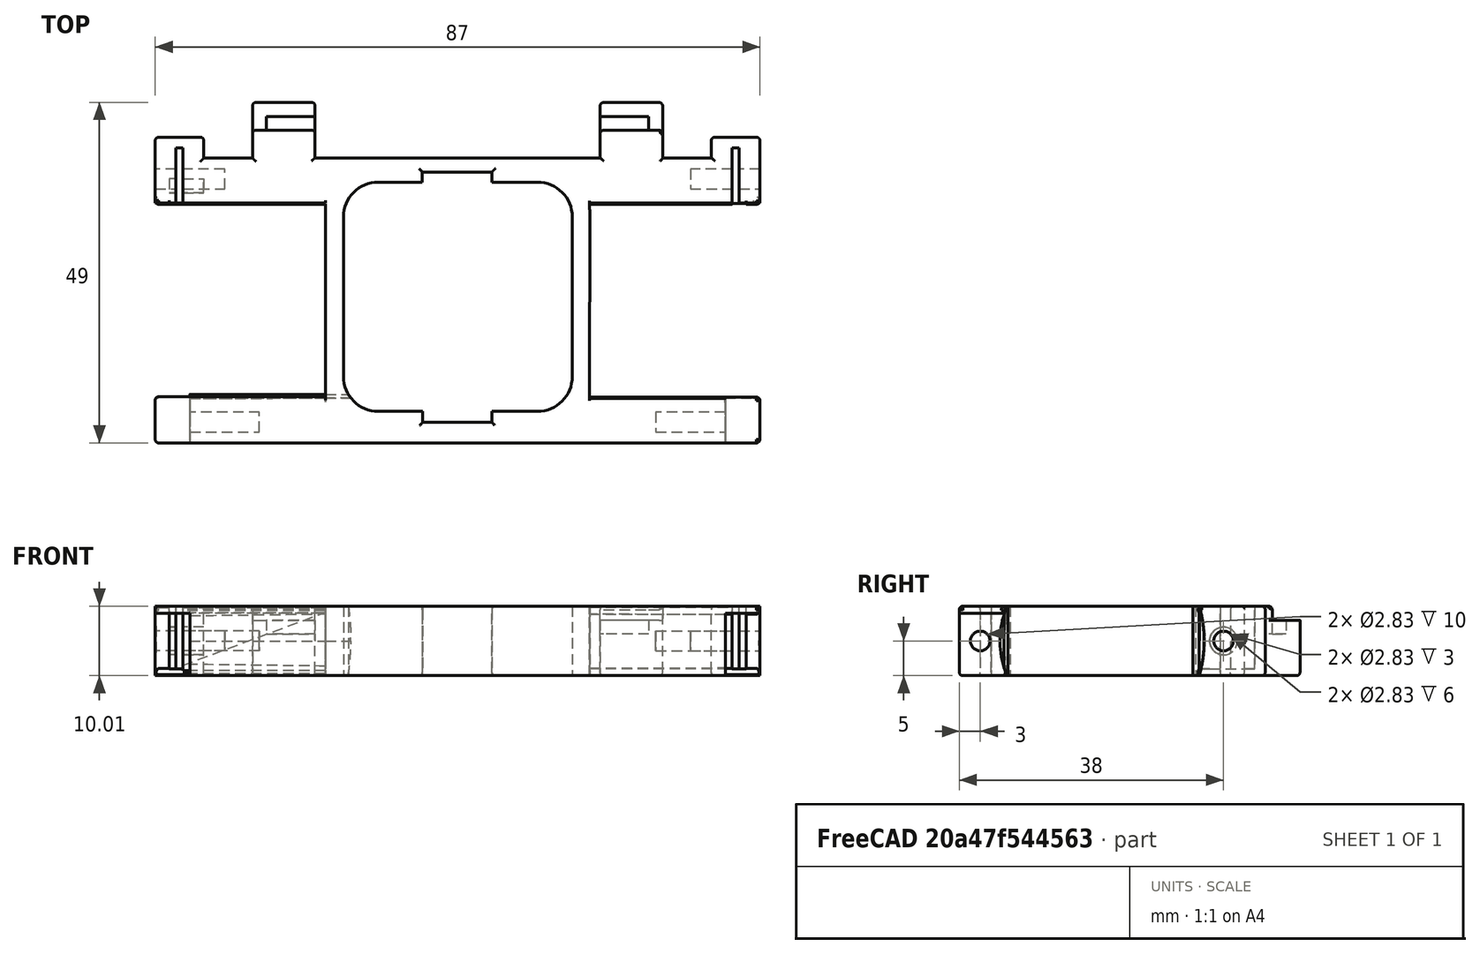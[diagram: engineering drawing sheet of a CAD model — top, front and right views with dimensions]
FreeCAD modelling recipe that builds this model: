
FCSTD DOCUMENT  (FreeCAD 0.18R16110 (Git))
Label: sop_motores
License: All rights reserved
LicenseURL: http://en.wikipedia.org/wiki/All_rights_reserved
objects: PartDesign::Fillet×64, Sketcher::SketchObject×41, PartDesign::Pocket×25, PartDesign::Pad×13, PartDesign::Body×1
note: 182 computed .brp shape members not serialized (recipe doc carries the construction recipe); baked Part::Feature solids carry a one-line shape summary decoded from their .brp

FEATURE [Sketcher::SketchObject] Sketch
  MapMode = 5
  Support = -> [XY_Plane]
  sketch-geometry (24):
    g0: LineSegment StartX=0 StartY=0 StartZ=0 EndX=7 EndY=0 EndZ=0
    g1: LineSegment StartX=7 StartY=0 StartZ=0 EndX=7 EndY=-3 EndZ=0
    g2: LineSegment StartX=7 StartY=-3 StartZ=0 EndX=14 EndY=-3 EndZ=0
    g3: LineSegment StartX=14 StartY=-3 StartZ=0 EndX=14 EndY=5 EndZ=0
    g4: LineSegment StartX=14 StartY=5 StartZ=0 EndX=23 EndY=5 EndZ=0
    g5: LineSegment StartX=23 StartY=5 StartZ=0 EndX=23 EndY=-3 EndZ=0
    g6: LineSegment StartX=23 StartY=-3 StartZ=0 EndX=64 EndY=-3 EndZ=0
    g7: LineSegment StartX=64 StartY=-3 StartZ=0 EndX=64 EndY=5 EndZ=0
    g8: LineSegment StartX=64 StartY=5 StartZ=0 EndX=73 EndY=5 EndZ=0
    g9: LineSegment StartX=73 StartY=5 StartZ=0 EndX=73 EndY=-3 EndZ=0
    g10: LineSegment StartX=73 StartY=-3 StartZ=0 EndX=80 EndY=-3 EndZ=0
    g11: LineSegment StartX=80 StartY=-3 StartZ=0 EndX=80 EndY=0 EndZ=0
    g12: LineSegment StartX=80 StartY=0 StartZ=0 EndX=87 EndY=0 EndZ=0
    g13: LineSegment StartX=87 StartY=0 StartZ=0 EndX=87 EndY=-10 EndZ=0
    g14: LineSegment StartX=87 StartY=-10 StartZ=0 EndX=62.5198 EndY=-10 EndZ=0
    g15: LineSegment StartX=62.4973 StartY=-37 StartZ=0 EndX=87 EndY=-37 EndZ=0
    g16: LineSegment StartX=87 StartY=-37 StartZ=0 EndX=87 EndY=-44 EndZ=0
    g17: LineSegment StartX=87 StartY=-44 StartZ=0 EndX=0 EndY=-44 EndZ=0
    g18: LineSegment StartX=0 StartY=-44 StartZ=0 EndX=0 EndY=-37 EndZ=0
    g19: LineSegment StartX=0 StartY=-37 StartZ=0 EndX=24.4807 EndY=-37 EndZ=0
    g20: LineSegment StartX=24.4807 StartY=-37 StartZ=0 EndX=24.5011 EndY=-10 EndZ=0
    g21: LineSegment StartX=24.5011 StartY=-10 StartZ=0 EndX=0 EndY=-10 EndZ=0
    g22: LineSegment StartX=62.5198 StartY=-10 StartZ=0 EndX=62.4973 EndY=-37 EndZ=0
    g23: LineSegment StartX=0 StartY=0 StartZ=0 EndX=0 EndY=-10 EndZ=0
  constraints (24):
    c: Coincident(g0,g1)
    c: Coincident(g1,g2)
    c: Coincident(g2,g3)
    c: Coincident(g3,g4)
    c: Coincident(g4,g5)
    c: Coincident(g5,g6)
    c: Coincident(g7,g8)
    c: Coincident(g8,g9)
    c: Coincident(g9,g10)
    c: Coincident(g10,g11)
    c: Coincident(g11,g12)
    c: Coincident(g12,g13)
    c: Coincident(g13,g14)
    c: Coincident(g15,g16)
    c: Coincident(g16,g17)
    c: Coincident(g18,g19)
    c: Coincident(g19,g20)
    c: Coincident(g20,g21)
    c: Coincident(g7,g6)
    c: Coincident(g17,g18)
    c: Coincident(g14,g22)
    c: Coincident(g15,g22)
    c: Coincident(g0,g23)
    c: Coincident(g21,g23)
FEATURE [PartDesign::Pad] Pad
  Length = 10
  Length2 = 100
  Profile = -> Sketch
  Type = 0
FEATURE [Sketcher::SketchObject] Sketch001
  MapMode = 5
  Placement = pos=(0,0,10) rot=(0,0,1;0rad)
  Support = -> [Pad]
  sketch-geometry (14):
    g0: LineSegment StartX=43.4694 StartY=-41 StartZ=0 EndX=38.4739 EndY=-41 EndZ=0
    g1: LineSegment StartX=38.4739 StartY=-41 StartZ=0 EndX=38.4739 EndY=-38 EndZ=0
    g2: LineSegment StartX=38.4739 StartY=-38 StartZ=0 EndX=28.4617 EndY=-38 EndZ=0
    g3: LineSegment StartX=28.4617 StartY=-38 StartZ=0 EndX=28.469 EndY=-8 EndZ=0
    g4: LineSegment StartX=28.469 StartY=-8 StartZ=0 EndX=38.4371 EndY=-8 EndZ=0
    g5: LineSegment StartX=38.4371 StartY=-8 StartZ=0 EndX=38.4371 EndY=-5 EndZ=0
    g6: LineSegment StartX=38.4371 StartY=-5 StartZ=0 EndX=48.4367 EndY=-5 EndZ=0
    g7: LineSegment StartX=48.4367 StartY=-5 StartZ=0 EndX=48.4367 EndY=-8 EndZ=0
    g8: LineSegment StartX=48.4367 StartY=-8 StartZ=0 EndX=58.4048 EndY=-8 EndZ=0
    g9: LineSegment StartX=58.4048 StartY=-8 StartZ=0 EndX=58.4159 EndY=-38 EndZ=0
    g10: LineSegment StartX=58.4159 StartY=-38 StartZ=0 EndX=48.4478 EndY=-38 EndZ=0
    g11: LineSegment StartX=48.4478 StartY=-38 StartZ=0 EndX=48.4478 EndY=-41 EndZ=0
    g12: LineSegment StartX=48.4478 StartY=-41 StartZ=0 EndX=43.4166 EndY=-41 EndZ=0
    g13: LineSegment StartX=43.4166 StartY=-41 StartZ=0 EndX=43.4694 EndY=-41 EndZ=0
  constraints (13):
    c: Coincident(g0,g1)
    c: Coincident(g1,g2)
    c: Coincident(g2,g3)
    c: Coincident(g3,g4)
    c: Coincident(g4,g5)
    c: Coincident(g5,g6)
    c: Coincident(g6,g7)
    c: Coincident(g7,g8)
    c: Coincident(g8,g9)
    c: Coincident(g9,g10)
    c: Coincident(g10,g11)
    c: Coincident(g11,g12)
    c: Coincident(g12,g13)
FEATURE [PartDesign::Pocket] Pocket
  BaseFeature = -> Pad
  Length = 10
  Length2 = 100
  Profile = -> Sketch001
  Type = 0
FEATURE [Sketcher::SketchObject] Sketch002
  MapMode = 5
  Placement = pos=(0,0,10) rot=(0,0,1;0rad)
  Support = -> [Pocket]
  sketch-geometry (8):
    g0: LineSegment StartX=23 StartY=1 StartZ=0 EndX=16 EndY=1 EndZ=0
    g1: LineSegment StartX=16 StartY=1 StartZ=0 EndX=16 EndY=3 EndZ=0
    g2: LineSegment StartX=16 StartY=3 StartZ=0 EndX=23 EndY=3 EndZ=0
    g3: LineSegment StartX=23 StartY=3 StartZ=0 EndX=23 EndY=1 EndZ=0
    g4: LineSegment StartX=64 StartY=1 StartZ=0 EndX=71 EndY=1 EndZ=0
    g5: LineSegment StartX=71 StartY=1 StartZ=0 EndX=71 EndY=3 EndZ=0
    g6: LineSegment StartX=71 StartY=3 StartZ=0 EndX=64 EndY=3 EndZ=0
    g7: LineSegment StartX=64 StartY=3 StartZ=0 EndX=64 EndY=1 EndZ=0
  constraints (6):
    c: Coincident(g0,g1)
    c: Coincident(g1,g2)
    c: Coincident(g2,g3)
    c: Coincident(g4,g5)
    c: Coincident(g5,g6)
    c: Coincident(g6,g7)
FEATURE [PartDesign::Pocket] Pocket001
  BaseFeature = -> Pocket
  Length = 5
  Length2 = 100
  Profile = -> Sketch002
  Type = 0
FEATURE [Sketcher::SketchObject] Sketch003
  MapMode = 5
  Placement = pos=(0,5,0) rot=(0,0.707107,0.707107;3.14159rad)
  Support = -> [Pocket001]
  sketch-geometry (8):
    g0: LineSegment StartX=-73 StartY=10 StartZ=0 EndX=-73 EndY=8 EndZ=0
    g1: LineSegment StartX=-73 StartY=8 StartZ=0 EndX=-64 EndY=8 EndZ=0
    g2: LineSegment StartX=-64 StartY=8 StartZ=0 EndX=-64 EndY=10 EndZ=0
    g3: LineSegment StartX=-64 StartY=10 StartZ=0 EndX=-73 EndY=10 EndZ=0
    g4: LineSegment StartX=-23 StartY=10 StartZ=0 EndX=-14 EndY=10 EndZ=0
    g5: LineSegment StartX=-14 StartY=10 StartZ=0 EndX=-14 EndY=8 EndZ=0
    g6: LineSegment StartX=-14 StartY=8 StartZ=0 EndX=-23 EndY=8 EndZ=0
    g7: LineSegment StartX=-23 StartY=8 StartZ=0 EndX=-23 EndY=10 EndZ=0
  constraints (8):
    c: Coincident(g0,g1)
    c: Coincident(g1,g2)
    c: Coincident(g2,g3)
    c: Coincident(g3,g0)
    c: Coincident(g4,g5)
    c: Coincident(g5,g6)
    c: Coincident(g6,g7)
    c: Coincident(g7,g4)
FEATURE [PartDesign::Pocket] Pocket002
  BaseFeature = -> Pocket001
  Length = 4
  Length2 = 100
  Profile = -> Sketch003
  Type = 0
FEATURE [Sketcher::SketchObject] Sketch004
  MapMode = 5
  Placement = pos=(87,0,0) rot=(0.57735,0.57735,0.57735;2.0944rad)
  Support = -> [Pocket002]
  sketch-geometry (2):
    g0: Circle CenterX=-6 CenterY=5 CenterZ=0 NormalX=0 NormalY=0 NormalZ=1 AngleXU=0 Radius=2
    g1: Circle CenterX=-41 CenterY=5 CenterZ=0 NormalX=0 NormalY=0 NormalZ=1 AngleXU=0 Radius=1.97023
FEATURE [PartDesign::Pocket] Pocket003
  BaseFeature = -> Pocket002
  Length = 12
  Length2 = 100
  Profile = -> Sketch004
  Type = 0
FEATURE [Sketcher::SketchObject] Sketch005
  MapMode = 5
  Placement = pos=(0,0,0) rot=(0.57735,-0.57735,-0.57735;2.0944rad)
  Support = -> [Pocket003]
  sketch-geometry (2):
    g0: Circle CenterX=6 CenterY=5 CenterZ=0 NormalX=0 NormalY=0 NormalZ=1 AngleXU=0 Radius=2
    g1: Circle CenterX=41 CenterY=5 CenterZ=0 NormalX=0 NormalY=0 NormalZ=1 AngleXU=0 Radius=2
FEATURE [PartDesign::Pocket] Pocket004
  BaseFeature = -> Pocket003
  Length = 12
  Length2 = 100
  Profile = -> Sketch005
  Type = 0
FEATURE [Sketcher::SketchObject] Sketch006
  MapMode = 5
  Placement = pos=(87,0,0) rot=(0.57735,0.57735,0.57735;2.0944rad)
  Support = -> [Pocket004]
  sketch-geometry (2):
    g0: ArcOfCircle CenterX=-24.8709 CenterY=5 CenterZ=0 NormalX=0 NormalY=0 NormalZ=1 AngleXU=0 Radius=13.2724 StartAngle=2.67251 EndAngle=3.61067
    g1: LineSegment StartX=-36.7097 StartY=11 StartZ=0 EndX=-36.7097 EndY=-0.999998 EndZ=0
  constraints (2):
    c: Coincident(g0,g1)
    c: Coincident(g0,g1)
FEATURE [PartDesign::Pocket] Pocket005
  BaseFeature = -> Pocket004
  Length = 24.5
  Length2 = 100
  Profile = -> Sketch006
  Type = 0
FEATURE [Sketcher::SketchObject] Sketch007
  MapMode = 5
  Placement = pos=(87,0,0) rot=(0.57735,0.57735,0.57735;2.0944rad)
  Support = -> [Pocket005]
  sketch-geometry (2):
    g0: ArcOfCircle CenterX=-22.2977 CenterY=5 CenterZ=0 NormalX=0 NormalY=0 NormalZ=1 AngleXU=0 Radius=13.3937 StartAngle=5.80677 EndAngle=6.75968
    g1: LineSegment StartX=-10.396 StartY=11.1433 StartZ=0 EndX=-10.3955 EndY=-1.14226 EndZ=0
  constraints (2):
    c: Coincident(g0,g1)
    c: Coincident(g0,g1)
FEATURE [PartDesign::Pocket] Pocket006
  BaseFeature = -> Pocket005
  Length = 24.5
  Length2 = 100
  Profile = -> Sketch007
  Type = 0
FEATURE [Sketcher::SketchObject] Sketch008
  MapMode = 5
  Placement = pos=(0,0,0) rot=(0.57735,-0.57735,-0.57735;2.0944rad)
  Support = -> [Pocket006]
  sketch-geometry (2):
    g0: ArcOfCircle CenterX=22.1388 CenterY=5.06289 CenterZ=0 NormalX=0 NormalY=0 NormalZ=1 AngleXU=0 Radius=13.2617 StartAngle=2.6721 EndAngle=3.61108
    g1: LineSegment StartX=10.312 StartY=11.0629 StartZ=0 EndX=10.312 EndY=-0.93711 EndZ=0
  constraints (2):
    c: Coincident(g0,g1)
    c: Coincident(g0,g1)
FEATURE [PartDesign::Pocket] Pocket007
  BaseFeature = -> Pocket006
  Length = 24.5
  Length2 = 100
  Profile = -> Sketch008
  Type = 0
FEATURE [Sketcher::SketchObject] Sketch009
  MapMode = 5
  Placement = pos=(0,0,0) rot=(0.57735,-0.57735,-0.57735;2.0944rad)
  Support = -> [Pocket007]
  sketch-geometry (2):
    g0: ArcOfCircle CenterX=24.8808 CenterY=5 CenterZ=0 NormalX=0 NormalY=0 NormalZ=1 AngleXU=0 Radius=13.2314 StartAngle=5.81253 EndAngle=6.75384
    g1: LineSegment StartX=36.6736 StartY=11 StartZ=0 EndX=36.6736 EndY=-1 EndZ=0
  constraints (2):
    c: Coincident(g0,g1)
    c: Coincident(g0,g1)
FEATURE [PartDesign::Pocket] Pocket008
  BaseFeature = -> Pocket007
  Length = 24.5
  Length2 = 100
  Profile = -> Sketch009
  Type = 0
FEATURE [Sketcher::SketchObject] Sketch010
  MapMode = 5
  Placement = pos=(0,0,10) rot=(0,0,1;0rad)
  Support = -> [Pocket008]
  sketch-geometry (8):
    g0: LineSegment StartX=2 StartY=-10 StartZ=0 EndX=4 EndY=-10 EndZ=0
    g1: LineSegment StartX=4 StartY=-10 StartZ=0 EndX=4 EndY=-3 EndZ=0
    g2: LineSegment StartX=4 StartY=-3 StartZ=0 EndX=2 EndY=-3 EndZ=0
    g3: LineSegment StartX=2 StartY=-3 StartZ=0 EndX=2 EndY=-10 EndZ=0
    g4: LineSegment StartX=83 StartY=-10 StartZ=0 EndX=85 EndY=-10 EndZ=0
    g5: LineSegment StartX=85 StartY=-10 StartZ=0 EndX=85 EndY=-3 EndZ=0
    g6: LineSegment StartX=85 StartY=-3 StartZ=0 EndX=83 EndY=-3 EndZ=0
    g7: LineSegment StartX=83 StartY=-3 StartZ=0 EndX=83 EndY=-10 EndZ=0
  constraints (8):
    c: Coincident(g0,g1)
    c: Coincident(g1,g2)
    c: Coincident(g2,g3)
    c: Coincident(g3,g0)
    c: Coincident(g4,g5)
    c: Coincident(g5,g6)
    c: Coincident(g6,g7)
    c: Coincident(g7,g4)
FEATURE [PartDesign::Pocket] Pocket009
  BaseFeature = -> Pocket008
  Length = 9
  Length2 = 100
  Profile = -> Sketch010
  Type = 0
FEATURE [PartDesign::Fillet] Fillet
  Base = -> Pocket009 [Edge64]
  BaseFeature = -> Pocket009
  Radius = 0.5
FEATURE [PartDesign::Fillet] Fillet001
  Base = -> Fillet [Edge7]
  BaseFeature = -> Fillet
  Radius = 0.5
FEATURE [PartDesign::Fillet] Fillet002
  Base = -> Fillet001 [Edge3]
  BaseFeature = -> Fillet001
  Radius = 0.5
FEATURE [PartDesign::Fillet] Fillet003
  Base = -> Fillet002 [Edge51]
  BaseFeature = -> Fillet002
  Radius = 0.5
FEATURE [PartDesign::Fillet] Fillet004
  Base = -> Fillet003 [Edge14]
  BaseFeature = -> Fillet003
  Radius = 0.5
FEATURE [PartDesign::Fillet] Fillet005
  Base = -> Fillet004 [Edge17]
  BaseFeature = -> Fillet004
  Radius = 0.5
FEATURE [PartDesign::Fillet] Fillet006
  Base = -> Fillet005 [Edge9]
  BaseFeature = -> Fillet005
  Radius = 0.4
FEATURE [PartDesign::Fillet] Fillet007
  Base = -> Fillet006 [Edge7]
  BaseFeature = -> Fillet006
  Radius = 0.4
FEATURE [PartDesign::Fillet] Fillet008
  Base = -> Fillet007 [Edge10]
  BaseFeature = -> Fillet007
  Radius = 0.4
FEATURE [PartDesign::Fillet] Fillet009
  Base = -> Fillet008 [Edge8]
  BaseFeature = -> Fillet008
  Radius = 0.5
FEATURE [PartDesign::Fillet] Fillet010
  Base = -> Fillet009 [Edge21]
  BaseFeature = -> Fillet009
  Radius = 0.5
FEATURE [PartDesign::Fillet] Fillet011
  Base = -> Fillet010 [Edge1]
  BaseFeature = -> Fillet010
  Radius = 0.5
FEATURE [PartDesign::Fillet] Fillet012
  Base = -> Fillet011 [Edge6]
  BaseFeature = -> Fillet011
  Radius = 0.5
FEATURE [PartDesign::Fillet] Fillet013
  Base = -> Fillet012 [Edge9]
  BaseFeature = -> Fillet012
  Radius = 0.5
FEATURE [PartDesign::Fillet] Fillet014
  Base = -> Fillet013 [Edge1]
  BaseFeature = -> Fillet013
  Radius = 0.4
FEATURE [PartDesign::Fillet] Fillet015
  Base = -> Fillet014 [Edge28]
  BaseFeature = -> Fillet014
  Radius = 0.54
FEATURE [PartDesign::Fillet] Fillet016
  Base = -> Fillet015 [Edge3]
  BaseFeature = -> Fillet015
  Radius = 0.5
FEATURE [PartDesign::Fillet] Fillet017
  Base = -> Fillet016 [Edge18]
  BaseFeature = -> Fillet016
  Radius = 0.5
FEATURE [PartDesign::Fillet] Fillet018
  Base = -> Fillet017 [Edge26]
  BaseFeature = -> Fillet017
  Radius = 0.5
FEATURE [PartDesign::Fillet] Fillet019
  Base = -> Fillet018 [Edge41]
  BaseFeature = -> Fillet018
  Radius = 0.5
FEATURE [PartDesign::Fillet] Fillet020
  Base = -> Fillet019 [Edge31]
  BaseFeature = -> Fillet019
  Radius = 0.5
FEATURE [PartDesign::Fillet] Fillet021
  Base = -> Fillet020 [Edge29]
  BaseFeature = -> Fillet020
  Radius = 0.5
FEATURE [PartDesign::Fillet] Fillet022
  Base = -> Fillet021 [Edge1]
  BaseFeature = -> Fillet021
  Radius = 0.5
FEATURE [PartDesign::Fillet] Fillet023
  Base = -> Fillet022 [Edge6]
  BaseFeature = -> Fillet022
  Radius = 0.5
FEATURE [PartDesign::Fillet] Fillet024
  Base = -> Fillet023 [Edge9]
  BaseFeature = -> Fillet023
  Radius = 0.5
FEATURE [PartDesign::Fillet] Fillet025
  Base = -> Fillet024 [Edge3]
  BaseFeature = -> Fillet024
  Radius = 0.5
FEATURE [PartDesign::Fillet] Fillet026
  Base = -> Fillet025 [Edge6]
  BaseFeature = -> Fillet025
  Radius = 0.5
FEATURE [PartDesign::Fillet] Fillet027
  Base = -> Fillet026 [Edge8]
  BaseFeature = -> Fillet026
  Radius = 0.5
FEATURE [PartDesign::Fillet] Fillet028
  Base = -> Fillet027 [Edge11]
  BaseFeature = -> Fillet027
  Radius = 0.5
FEATURE [PartDesign::Fillet] Fillet029
  Base = -> Fillet028 [Edge1]
  BaseFeature = -> Fillet028
  Radius = 0.5
FEATURE [PartDesign::Fillet] Fillet030
  Base = -> Fillet029 [Edge6]
  BaseFeature = -> Fillet029
  Radius = 0.4
FEATURE [PartDesign::Fillet] Fillet031
  Base = -> Fillet030 [Edge2]
  BaseFeature = -> Fillet030
  Radius = 0.3
FEATURE [PartDesign::Fillet] Fillet032
  Base = -> Fillet031 [Edge3]
  BaseFeature = -> Fillet031
  Radius = 0.5
FEATURE [PartDesign::Fillet] Fillet033
  Base = -> Fillet032 [Edge10]
  BaseFeature = -> Fillet032
  Radius = 0.4
FEATURE [PartDesign::Fillet] Fillet034
  Base = -> Fillet033 [Edge152]
  BaseFeature = -> Fillet033
  Radius = 0.5
FEATURE [PartDesign::Fillet] Fillet035
  Base = -> Fillet034 [Edge12]
  BaseFeature = -> Fillet034
  Radius = 0.5
FEATURE [PartDesign::Fillet] Fillet036
  Base = -> Fillet035 [Edge71]
  BaseFeature = -> Fillet035
  Radius = 0.5
FEATURE [PartDesign::Fillet] Fillet037
  Base = -> Fillet036 [Edge1]
  BaseFeature = -> Fillet036
  Radius = 0.5
FEATURE [PartDesign::Fillet] Fillet038
  Base = -> Fillet037 [Edge24]
  BaseFeature = -> Fillet037
  Radius = 0.5
FEATURE [PartDesign::Fillet] Fillet039
  Base = -> Fillet038 [Edge3]
  BaseFeature = -> Fillet038
  Radius = 0.5
FEATURE [PartDesign::Fillet] Fillet040
  Base = -> Fillet039 [Edge8]
  BaseFeature = -> Fillet039
  Radius = 0.5
FEATURE [PartDesign::Fillet] Fillet041
  Base = -> Fillet040 [Edge3]
  BaseFeature = -> Fillet040
  Radius = 0.5
FEATURE [PartDesign::Fillet] Fillet042
  Base = -> Fillet041 [Edge6]
  BaseFeature = -> Fillet041
  Radius = 0.4
FEATURE [PartDesign::Fillet] Fillet043
  Base = -> Fillet042 [Edge31]
  BaseFeature = -> Fillet042
  Radius = 0.4
FEATURE [PartDesign::Fillet] Fillet044
  Base = -> Fillet043 [Edge4]
  BaseFeature = -> Fillet043
  Radius = 0.5
FEATURE [PartDesign::Fillet] Fillet045
  Base = -> Fillet044 [Edge14]
  BaseFeature = -> Fillet044
  Radius = 0.5
FEATURE [PartDesign::Fillet] Fillet046
  Base = -> Fillet045 [Edge61]
  BaseFeature = -> Fillet045
  Radius = 0.5
FEATURE [PartDesign::Fillet] Fillet047
  Base = -> Fillet046 [Edge16]
  BaseFeature = -> Fillet046
  Radius = 0.5
FEATURE [PartDesign::Fillet] Fillet048
  Base = -> Fillet047 [Edge26]
  BaseFeature = -> Fillet047
  Radius = 0.4
FEATURE [PartDesign::Fillet] Fillet049
  Base = -> Fillet048 [Edge62]
  BaseFeature = -> Fillet048
  Radius = 0.5
FEATURE [PartDesign::Fillet] Fillet050
  Base = -> Fillet049 [Edge6]
  BaseFeature = -> Fillet049
  Radius = 0.5
FEATURE [PartDesign::Fillet] Fillet051
  Base = -> Fillet050 [Edge16]
  BaseFeature = -> Fillet050
  Radius = 0.49
FEATURE [PartDesign::Fillet] Fillet052
  Base = -> Fillet051 [Edge15]
  BaseFeature = -> Fillet051
  Radius = 0.49
FEATURE [PartDesign::Fillet] Fillet053
  Base = -> Fillet052 [Edge13]
  BaseFeature = -> Fillet052
  Radius = 0.39
FEATURE [PartDesign::Fillet] Fillet054
  Base = -> Fillet053 [Edge26]
  BaseFeature = -> Fillet053
  Radius = 0.39
FEATURE [PartDesign::Fillet] Fillet055
  Base = -> Fillet054 [Edge69]
  BaseFeature = -> Fillet054
  Radius = 0.5
FEATURE [Sketcher::SketchObject] Sketch011
  MapMode = 5
  Placement = pos=(0,0,0) rot=(1,0,0;3.14159rad)
  Support = -> [Fillet055]
  sketch-geometry (8):
    g0: LineSegment StartX=0 StartY=44 StartZ=0 EndX=1 EndY=44 EndZ=0
    g1: LineSegment StartX=1 StartY=44 StartZ=0 EndX=1 EndY=37 EndZ=0
    g2: LineSegment StartX=1 StartY=37 StartZ=0 EndX=0 EndY=37 EndZ=0
    g3: LineSegment StartX=0 StartY=37 StartZ=0 EndX=0 EndY=44 EndZ=0
    g4: LineSegment StartX=86 StartY=44 StartZ=0 EndX=87 EndY=44 EndZ=0
    g5: LineSegment StartX=87 StartY=44 StartZ=0 EndX=87 EndY=37 EndZ=0
    g6: LineSegment StartX=87 StartY=37 StartZ=0 EndX=86 EndY=37 EndZ=0
    g7: LineSegment StartX=86 StartY=37 StartZ=0 EndX=86 EndY=44 EndZ=0
  constraints (8):
    c: Coincident(g0,g1)
    c: Coincident(g1,g2)
    c: Coincident(g2,g3)
    c: Coincident(g3,g0)
    c: Coincident(g4,g5)
    c: Coincident(g5,g6)
    c: Coincident(g6,g7)
    c: Coincident(g7,g4)
FEATURE [PartDesign::Pocket] Pocket010
  BaseFeature = -> Fillet055
  Length = 9
  Length2 = 100
  Profile = -> Sketch011
  Type = 0
FEATURE [PartDesign::Fillet] Fillet056
  Base = -> Pocket010 [Edge442]
  BaseFeature = -> Pocket010
  Radius = 5
FEATURE [PartDesign::Fillet] Fillet057
  Base = -> Fillet056 [Edge461]
  BaseFeature = -> Fillet056
  Radius = 5
FEATURE [PartDesign::Fillet] Fillet058
  Base = -> Fillet057 [Edge477]
  BaseFeature = -> Fillet057
  Radius = 5
FEATURE [PartDesign::Fillet] Fillet059
  Base = -> Fillet058 [Edge487]
  BaseFeature = -> Fillet058
  Radius = 5
FEATURE [Sketcher::SketchObject] Sketch012
  MapMode = 5
  Placement = pos=(0,0,10) rot=(0,0,1;0rad)
  Support = -> [Fillet059]
  sketch-geometry (4):
    g0: LineSegment StartX=27.0787 StartY=-6.46494 StartZ=0 EndX=60 EndY=-6.46494 EndZ=0
    g1: LineSegment StartX=60 StartY=-6.46494 StartZ=0 EndX=60 EndY=-39.4522 EndZ=0
    g2: LineSegment StartX=60 StartY=-39.4522 StartZ=0 EndX=27.0787 EndY=-39.4522 EndZ=0
    g3: LineSegment StartX=27.0787 StartY=-39.4522 StartZ=0 EndX=27.0787 EndY=-6.46494 EndZ=0
  constraints (8):
    c: Coincident(g0,g1)
    c: Coincident(g1,g2)
    c: Coincident(g2,g3)
    c: Coincident(g3,g0)
    c: Horizontal(g0)
    c: Horizontal(g2)
    c: Vertical(g1)
    c: Vertical(g3)
FEATURE [PartDesign::Pocket] Pocket011
  BaseFeature = -> Fillet059
  Length = 10
  Length2 = 100
  Profile = -> Sketch012
  Type = 0
FEATURE [PartDesign::Fillet] Fillet060
  Base = -> Pocket011 [Edge187]
  BaseFeature = -> Pocket011
  Radius = 5
FEATURE [PartDesign::Fillet] Fillet061
  Base = -> Fillet060 [Edge107]
  BaseFeature = -> Fillet060
  Radius = 5
FEATURE [PartDesign::Fillet] Fillet062
  Base = -> Fillet061 [Edge114]
  BaseFeature = -> Fillet061
  Radius = 5
FEATURE [PartDesign::Fillet] Fillet063
  Base = -> Fillet062 [Edge117]
  BaseFeature = -> Fillet062
  Radius = 5
FEATURE [Sketcher::SketchObject] Sketch013
  MapMode = 5
  Placement = pos=(0,0,10) rot=(0,0,1;0rad)
  Support = -> [Fillet063]
  sketch-geometry (8):
    g0: LineSegment StartX=2 StartY=-3 StartZ=0 EndX=4 EndY=-3 EndZ=0
    g1: LineSegment StartX=4 StartY=-3 StartZ=0 EndX=4 EndY=-1.53185 EndZ=0
    g2: LineSegment StartX=4 StartY=-1.53185 StartZ=0 EndX=2 EndY=-1.53185 EndZ=0
    g3: LineSegment StartX=2 StartY=-1.53185 StartZ=0 EndX=2 EndY=-3 EndZ=0
    g4: LineSegment StartX=83 StartY=-3 StartZ=0 EndX=85 EndY=-3 EndZ=0
    g5: LineSegment StartX=85 StartY=-3 StartZ=0 EndX=85 EndY=-1.50986 EndZ=0
    g6: LineSegment StartX=85 StartY=-1.50986 StartZ=0 EndX=83 EndY=-1.50986 EndZ=0
    g7: LineSegment StartX=83 StartY=-1.50986 StartZ=0 EndX=83 EndY=-3 EndZ=0
  constraints (16):
    c: Coincident(g0,g1)
    c: Coincident(g1,g2)
    c: Coincident(g2,g3)
    c: Coincident(g3,g0)
    c: Horizontal(g0)
    c: Horizontal(g2)
    c: Vertical(g1)
    c: Vertical(g3)
    c: Coincident(g4,g5)
    c: Coincident(g5,g6)
    c: Coincident(g6,g7)
    c: Coincident(g7,g4)
    c: Horizontal(g4)
    c: Horizontal(g6)
    c: Vertical(g5)
    c: Vertical(g7)
FEATURE [PartDesign::Pocket] Pocket012
  BaseFeature = -> Fillet063
  Length = 9
  Length2 = 100
  Profile = -> Sketch013
  Type = 0
FEATURE [Sketcher::SketchObject] Sketch014
  MapMode = 5
  Placement = pos=(1,0,0) rot=(0.57735,-0.57735,-0.57735;2.0944rad)
  Support = -> [Pocket012]
  sketch-geometry (4):
    g0: LineSegment StartX=44 StartY=0 StartZ=0 EndX=44 EndY=9 EndZ=0
    g1: LineSegment StartX=44 StartY=9 StartZ=0 EndX=37 EndY=9 EndZ=0
    g2: LineSegment StartX=37 StartY=9 StartZ=0 EndX=37 EndY=0 EndZ=0
    g3: LineSegment StartX=37 StartY=0 StartZ=0 EndX=44 EndY=0 EndZ=0
  constraints (4):
    c: Coincident(g0,g1)
    c: Coincident(g1,g2)
    c: Coincident(g2,g3)
    c: Coincident(g3,g0)
FEATURE [PartDesign::Pocket] Pocket013
  BaseFeature = -> Pocket012
  Length = 4
  Length2 = 100
  Profile = -> Sketch014
  Type = 0
FEATURE [Sketcher::SketchObject] Sketch015
  MapMode = 5
  Placement = pos=(86,0,0) rot=(0.57735,0.57735,0.57735;2.0944rad)
  Support = -> [Pocket013]
  sketch-geometry (4):
    g0: LineSegment StartX=-44 StartY=9 StartZ=0 EndX=-37 EndY=9 EndZ=0
    g1: LineSegment StartX=-37 StartY=9 StartZ=0 EndX=-37 EndY=0 EndZ=0
    g2: LineSegment StartX=-37 StartY=0 StartZ=0 EndX=-44 EndY=0 EndZ=0
    g3: LineSegment StartX=-44 StartY=0 StartZ=0 EndX=-44 EndY=9 EndZ=0
  constraints (4):
    c: Coincident(g0,g1)
    c: Coincident(g1,g2)
    c: Coincident(g2,g3)
    c: Coincident(g3,g0)
FEATURE [PartDesign::Pocket] Pocket014
  BaseFeature = -> Pocket013
  Length = 4
  Length2 = 100
  Profile = -> Sketch015
  Type = 0
FEATURE [Sketcher::SketchObject] Sketch016
  MapMode = 5
  Placement = pos=(62.5281,-0.0521484,0) rot=(0.577671,0.57719,0.57719;2.09391rad)
  Support = -> [Pocket014]
  sketch-geometry (2):
    g0: LineSegment StartX=-37.5 StartY=-2.18812e-11 StartZ=0 EndX=-37.5259 EndY=10 EndZ=0
    g1: ArcOfCircle CenterX=-18.8886 CenterY=5.04815 CenterZ=0 NormalX=0 NormalY=0 NormalZ=1 AngleXU=0 Radius=19.2839 StartAngle=2.8819 EndAngle=3.40646
  constraints (2):
    c: Coincident(g1,g0)
    c: Coincident(g0,g1)
FEATURE [PartDesign::Pad] Pad001
  BaseFeature = -> Pocket014
  Length = 19.5
  Length2 = 100
  Profile = -> Sketch016
  Type = 0
FEATURE [Sketcher::SketchObject] Sketch017
  MapMode = 5
  Placement = pos=(62.5,0,0) rot=(0.57735,0.57735,0.57735;2.0944rad)
  Support = -> [Pad001]
  sketch-geometry (2):
    g0: LineSegment StartX=-9.47195 StartY=10 StartZ=0 EndX=-9.5 EndY=-3.1557e-11 EndZ=0
    g1: ArcOfCircle CenterX=-27.0658 CenterY=5.0493 CenterZ=0 NormalX=0 NormalY=0 NormalZ=1 AngleXU=0 Radius=18.2771 StartAngle=6.00328 EndAngle=6.55748
  constraints (2):
    c: Coincident(g0,g1)
    c: Coincident(g0,g1)
FEATURE [PartDesign::Pad] Pad002
  BaseFeature = -> Pad001
  Length = 24.5
  Length2 = 100
  Profile = -> Sketch017
  Type = 0
FEATURE [Sketcher::SketchObject] Sketch018
  MapMode = 5
  Placement = pos=(0,0,10) rot=(0,0,1;0rad)
  Support = -> [Pad002]
  sketch-geometry (4):
    g0: LineSegment StartX=83 StartY=-8 StartZ=0 EndX=85 EndY=-8 EndZ=0
    g1: LineSegment StartX=85 StartY=-8 StartZ=0 EndX=85 EndY=-10 EndZ=0
    g2: LineSegment StartX=85 StartY=-10 StartZ=0 EndX=83 EndY=-10 EndZ=0
    g3: LineSegment StartX=83 StartY=-10 StartZ=0 EndX=83 EndY=-8 EndZ=0
  constraints (4):
    c: Coincident(g0,g1)
    c: Coincident(g1,g2)
    c: Coincident(g2,g3)
    c: Coincident(g3,g0)
FEATURE [PartDesign::Pocket] Pocket015
  BaseFeature = -> Pad002
  Length = 9
  Length2 = 100
  Profile = -> Sketch018
  Type = 0
FEATURE [Sketcher::SketchObject] Sketch019
  MapMode = 5
  Placement = pos=(24.5087,-0.0185195,0) rot=(-0.577059,0.577496,0.577496;4.18835rad)
  Support = -> [Pocket015]
  sketch-geometry (2):
    g0: LineSegment StartX=9.5 StartY=1.8e-15 StartZ=0 EndX=9.47975 EndY=10.0065 EndZ=0
    g1: ArcOfCircle CenterX=24.7722 CenterY=5.03418 CenterZ=0 NormalX=0 NormalY=0 NormalZ=1 AngleXU=0 Radius=16.0805 StartAngle=2.82723 EndAngle=3.46001
  constraints (2):
    c: Coincident(g0,g1)
    c: Coincident(g0,g1)
FEATURE [PartDesign::Pad] Pad003
  BaseFeature = -> Pocket015
  Length = 24.5
  Length2 = 100
  Profile = -> Sketch019
  Type = 0
FEATURE [Sketcher::SketchObject] Sketch020
  MapMode = 5
  Placement = pos=(0,0,10) rot=(0,0,1;0rad)
  Support = -> [Pad003]
  sketch-geometry (4):
    g0: LineSegment StartX=2 StartY=-8 StartZ=0 EndX=4 EndY=-8 EndZ=0
    g1: LineSegment StartX=4 StartY=-8 StartZ=0 EndX=4 EndY=-10 EndZ=0
    g2: LineSegment StartX=4 StartY=-10 StartZ=0 EndX=2 EndY=-10 EndZ=0
    g3: LineSegment StartX=2 StartY=-10 StartZ=0 EndX=2 EndY=-8 EndZ=0
  constraints (4):
    c: Coincident(g0,g1)
    c: Coincident(g1,g2)
    c: Coincident(g2,g3)
    c: Coincident(g3,g0)
FEATURE [PartDesign::Pocket] Pocket016
  BaseFeature = -> Pad003
  Length = 9
  Length2 = 100
  Profile = -> Sketch020
  Type = 0
FEATURE [Sketcher::SketchObject] Sketch021
  MapMode = 5
  Placement = pos=(24.5087,-0.0185195,0) rot=(-0.577059,0.577496,0.577496;4.18835rad)
  Support = -> [Pocket016]
  sketch-geometry (2):
    g0: LineSegment StartX=37 StartY=-3.6e-15 StartZ=0 EndX=37.02 EndY=10.0097 EndZ=0
    g1: ArcOfCircle CenterX=27.1332 CenterY=5.02455 CenterZ=0 NormalX=0 NormalY=0 NormalZ=1 AngleXU=0 Radius=11.0725 StartAngle=5.81217 EndAngle=6.75021
  constraints (2):
    c: Coincident(g1,g0)
    c: Coincident(g1,g0)
FEATURE [PartDesign::Pad] Pad004
  BaseFeature = -> Pocket016
  Length = 19.5
  Length2 = 100
  Profile = -> Sketch021
  Type = 0
FEATURE [Sketcher::SketchObject] Sketch022
  MapMode = 5
  Placement = pos=(0,0,5) rot=(0,0,1;0rad)
  Support = -> [Pad004]
  sketch-geometry (8):
    g0: LineSegment StartX=16 StartY=3 StartZ=0 EndX=16 EndY=0.512637 EndZ=0
    g1: LineSegment StartX=16 StartY=0.512637 StartZ=0 EndX=23 EndY=0.45612 EndZ=0
    g2: LineSegment StartX=23 StartY=0.45612 StartZ=0 EndX=23 EndY=3 EndZ=0
    g3: LineSegment StartX=23 StartY=3 StartZ=0 EndX=16 EndY=3 EndZ=0
    g4: LineSegment StartX=71 StartY=3 StartZ=0 EndX=64 EndY=3 EndZ=0
    g5: LineSegment StartX=64 StartY=3 StartZ=0 EndX=64 EndY=0.483334 EndZ=0
    g6: LineSegment StartX=64 StartY=0.483334 StartZ=0 EndX=71 EndY=0.483334 EndZ=0
    g7: LineSegment StartX=71 StartY=0.483334 StartZ=0 EndX=71 EndY=3 EndZ=0
  constraints (8):
    c: Coincident(g0,g1)
    c: Coincident(g1,g2)
    c: Coincident(g2,g3)
    c: Coincident(g3,g0)
    c: Coincident(g4,g5)
    c: Coincident(g5,g6)
    c: Coincident(g6,g7)
    c: Coincident(g7,g4)
FEATURE [PartDesign::Pad] Pad005
  BaseFeature = -> Pad004
  Length = 1
  Length2 = 100
  Profile = -> Sketch022
  Type = 0
FEATURE [Sketcher::SketchObject] Sketch023
  MapMode = 5
  Placement = pos=(62.5281,-0.0521484,0) rot=(0.577671,0.57719,0.57719;2.09391rad)
  Support = -> [Pad005]
FEATURE [Sketcher::SketchObject] Sketch024
  MapMode = 5
  Placement = pos=(24.5087,-0.0185195,0) rot=(-0.577059,0.577496,0.577496;4.18835rad)
  Support = -> [Pad005]
FEATURE [Sketcher::SketchObject] Sketch025
  MapMode = 5
  Placement = pos=(5.00867,-0.0037847,-1.2e-15) rot=(-0.577059,0.577496,0.577496;4.18835rad)
  Support = -> [Pad005]
  sketch-geometry (3):
    g0: LineSegment StartX=36.99 StartY=0 StartZ=0 EndX=36.9935 EndY=9.99852 EndZ=0
    g1: ArcOfCircle CenterX=16.6778 CenterY=4.56607 CenterZ=0 NormalX=0 NormalY=0 NormalZ=1 AngleXU=0 Radius=20.8191 StartAngle=6.06207 EndAngle=6.30397
    g2: ArcOfCircle CenterX=16.9079 CenterY=5.46967 CenterZ=0 NormalX=0 NormalY=0 NormalZ=1 AngleXU=0 Radius=20.5899 StartAngle=6.26031 EndAngle=6.50495
  constraints (3):
    c: Coincident(g0,g2)
    c: Coincident(g0,g1)
    c: Coincident(g1,g2)
FEATURE [PartDesign::Pocket] Pocket017
  BaseFeature = -> Pad005
  Length = 24
  Length2 = 100
  Profile = -> Sketch025
  Type = 0
FEATURE [Sketcher::SketchObject] Sketch026
  MapMode = 5
  Placement = pos=(0,0,1) rot=(0,0,1;0rad)
  Support = -> [Pocket017]
  sketch-geometry (4):
    g0: LineSegment StartX=2 StartY=-1 StartZ=0 EndX=3 EndY=-1 EndZ=0
    g1: LineSegment StartX=3 StartY=-1 StartZ=0 EndX=2.9979 EndY=-9.49658 EndZ=0
    g2: LineSegment StartX=2.9979 StartY=-9.49658 StartZ=0 EndX=1.9979 EndY=-9.50293 EndZ=0
    g3: LineSegment StartX=1.9979 StartY=-9.50293 StartZ=0 EndX=2 EndY=-1 EndZ=0
  constraints (4):
    c: Coincident(g0,g1)
    c: Coincident(g1,g2)
    c: Coincident(g2,g3)
    c: Coincident(g3,g0)
FEATURE [PartDesign::Pad] Pad006
  BaseFeature = -> Pocket017
  Length = 9
  Length2 = 100
  Profile = -> Sketch026
  Type = 0
FEATURE [Sketcher::SketchObject] Sketch027
  MapMode = 5
  Placement = pos=(0,0,1) rot=(0,0,1;0rad)
  Support = -> [Pad006]
  sketch-geometry (4):
    g0: LineSegment StartX=84 StartY=-1 StartZ=0 EndX=85 EndY=-1 EndZ=0
    g1: LineSegment StartX=85 StartY=-1 StartZ=0 EndX=85 EndY=-9.49425 EndZ=0
    g2: LineSegment StartX=85 StartY=-9.49425 StartZ=0 EndX=84 EndY=-9.49554 EndZ=0
    g3: LineSegment StartX=84 StartY=-9.49554 StartZ=0 EndX=84 EndY=-1 EndZ=0
  constraints (4):
    c: Coincident(g0,g1)
    c: Coincident(g1,g2)
    c: Coincident(g2,g3)
    c: Coincident(g3,g0)
FEATURE [PartDesign::Pad] Pad007
  BaseFeature = -> Pad006
  Length = 9
  Length2 = 100
  Profile = -> Sketch027
  Type = 0
FEATURE [Sketcher::SketchObject] Sketch028
  MapMode = 5
  Placement = pos=(85,0,0) rot=(0.57735,0.57735,0.57735;2.0944rad)
  Support = -> [Pad007]
  sketch-geometry (1):
    g0: Circle CenterX=-6 CenterY=5 CenterZ=0 NormalX=0 NormalY=0 NormalZ=1 AngleXU=0 Radius=2
FEATURE [PartDesign::Pocket] Pocket018
  BaseFeature = -> Pad007
  Length = 5
  Length2 = 100
  Profile = -> Sketch028
  Type = 0
FEATURE [Sketcher::SketchObject] Sketch029
  MapMode = 5
  Placement = pos=(2.00025,-0.000493303,0) rot=(-0.577255,0.577398,0.577398;4.18865rad)
  Support = -> [Pocket018]
  sketch-geometry (1):
    g0: Circle CenterX=6 CenterY=5 CenterZ=0 NormalX=0 NormalY=0 NormalZ=1 AngleXU=0 Radius=2
FEATURE [PartDesign::Pocket] Pocket019
  BaseFeature = -> Pocket018
  Length = 5
  Length2 = 100
  Profile = -> Sketch029
  Type = 0
FEATURE [Sketcher::SketchObject] Sketch030
  MapMode = 5
  Placement = pos=(12,0,0) rot=(0.57735,-0.57735,-0.57735;2.0944rad)
  Support = -> [Pocket019]
  sketch-geometry (1):
    g0: Circle CenterX=6 CenterY=5 CenterZ=0 NormalX=0 NormalY=0 NormalZ=1 AngleXU=0 Radius=2
FEATURE [PartDesign::Pad] Pad008
  BaseFeature = -> Pocket019
  Length = 12
  Length2 = 100
  Profile = -> Sketch030
  Type = 0
FEATURE [Sketcher::SketchObject] Sketch031
  MapMode = 5
  Placement = pos=(75,0,0) rot=(0.57735,0.57735,0.57735;2.0944rad)
  Support = -> [Pad008]
  sketch-geometry (1):
    g0: Circle CenterX=-6 CenterY=5 CenterZ=0 NormalX=0 NormalY=0 NormalZ=1 AngleXU=0 Radius=2.03849
FEATURE [PartDesign::Pad] Pad009
  BaseFeature = -> Pad008
  Length = 12
  Length2 = 100
  Profile = -> Sketch031
  Type = 0
FEATURE [Sketcher::SketchObject] Sketch032
  MapMode = 5
  Placement = pos=(0,0,10) rot=(0,0,1;0rad)
  Support = -> [Pad009]
  sketch-geometry (8):
    g0: LineSegment StartX=83 StartY=-3 StartZ=0 EndX=84 EndY=-3 EndZ=0
    g1: LineSegment StartX=84 StartY=-3 StartZ=0 EndX=84 EndY=-9 EndZ=0
    g2: LineSegment StartX=84 StartY=-9 StartZ=0 EndX=83 EndY=-9 EndZ=0
    g3: LineSegment StartX=83 StartY=-9 StartZ=0 EndX=83 EndY=-3 EndZ=0
    g4: LineSegment StartX=3 StartY=-3 StartZ=0 EndX=4 EndY=-3 EndZ=0
    g5: LineSegment StartX=4 StartY=-3 StartZ=0 EndX=4 EndY=-9 EndZ=0
    g6: LineSegment StartX=4 StartY=-9 StartZ=0 EndX=3 EndY=-9 EndZ=0
    g7: LineSegment StartX=3 StartY=-9 StartZ=0 EndX=3 EndY=-3 EndZ=0
  constraints (8):
    c: Coincident(g0,g1)
    c: Coincident(g1,g2)
    c: Coincident(g2,g3)
    c: Coincident(g3,g0)
    c: Coincident(g4,g5)
    c: Coincident(g5,g6)
    c: Coincident(g6,g7)
    c: Coincident(g7,g4)
FEATURE [PartDesign::Pocket] Pocket020
  BaseFeature = -> Pad009
  Length = 9
  Length2 = 100
  Profile = -> Sketch032
  Type = 0
FEATURE [Sketcher::SketchObject] Sketch033
  MapMode = 5
  Placement = pos=(24.5,0,0) rot=(0.57735,-0.57735,-0.57735;2.0944rad)
  Support = -> [Pocket020]
  sketch-geometry (4):
    g0: LineSegment StartX=9.5 StartY=10 StartZ=0 EndX=9.6 EndY=10 EndZ=0
    g1: LineSegment StartX=9.6 StartY=10 StartZ=0 EndX=9.6 EndY=0 EndZ=0
    g2: LineSegment StartX=9.6 StartY=0 StartZ=0 EndX=9.5 EndY=0 EndZ=0
    g3: LineSegment StartX=9.5 StartY=0 StartZ=0 EndX=9.5 EndY=10 EndZ=0
  constraints (4):
    c: Coincident(g0,g1)
    c: Coincident(g1,g2)
    c: Coincident(g2,g3)
    c: Coincident(g3,g0)
FEATURE [PartDesign::Pad] Pad010
  BaseFeature = -> Pocket020
  Length = 20.5
  Length2 = 100
  Profile = -> Sketch033
  Type = 0
FEATURE [Sketcher::SketchObject] Sketch034
  MapMode = 5
  Placement = pos=(75,0,0) rot=(0.57735,0.57735,0.57735;2.0944rad)
  Support = -> [Pad010]
  sketch-geometry (1):
    g0: Circle CenterX=-41 CenterY=5 CenterZ=0 NormalX=0 NormalY=0 NormalZ=1 AngleXU=0 Radius=2
FEATURE [PartDesign::Pad] Pad011
  BaseFeature = -> Pad010
  Length = 7
  Length2 = 100
  Profile = -> Sketch034
  Type = 0
FEATURE [Sketcher::SketchObject] Sketch035
  MapMode = 5
  Placement = pos=(12,0,0) rot=(0.57735,-0.57735,-0.57735;2.0944rad)
  Support = -> [Pad011]
  sketch-geometry (1):
    g0: Circle CenterX=41 CenterY=5 CenterZ=0 NormalX=0 NormalY=0 NormalZ=1 AngleXU=0 Radius=2
FEATURE [PartDesign::Pad] Pad012
  BaseFeature = -> Pad011
  Length = 7
  Length2 = 100
  Profile = -> Sketch035
  Type = 0
FEATURE [Sketcher::SketchObject] Sketch036
  MapMode = 5
  Placement = pos=(87,0,0) rot=(0.57735,0.57735,0.57735;2.0944rad)
  Support = -> [Pad012]
  sketch-geometry (1):
    g0: Circle CenterX=-6 CenterY=5 CenterZ=0 NormalX=0 NormalY=0 NormalZ=1 AngleXU=0 Radius=1.41421
FEATURE [PartDesign::Pocket] Pocket021
  BaseFeature = -> Pad012
  Length = 10
  Length2 = 100
  Profile = -> Sketch036
  Type = 0
FEATURE [Sketcher::SketchObject] Sketch037
  MapMode = 5
  Placement = pos=(82,0,0) rot=(0.57735,0.57735,0.57735;2.0944rad)
  Support = -> [Pocket021]
  sketch-geometry (1):
    g0: Circle CenterX=-41 CenterY=5 CenterZ=0 NormalX=0 NormalY=0 NormalZ=1 AngleXU=0 Radius=1.41421
FEATURE [PartDesign::Pocket] Pocket022
  BaseFeature = -> Pocket021
  Length = 10
  Length2 = 100
  Profile = -> Sketch037
  Type = 0
FEATURE [Sketcher::SketchObject] Sketch038
  MapMode = 5
  Placement = pos=(3,0,0) rot=(0.57735,0.57735,0.57735;2.0944rad)
  Support = -> [Pocket022]
FEATURE [Sketcher::SketchObject] Sketch039
  MapMode = 5
  Placement = pos=(1.8e-15,0,0) rot=(0.57735,-0.57735,-0.57735;2.0944rad)
  Support = -> [Pocket022]
  sketch-geometry (1):
    g0: Circle CenterX=6 CenterY=5 CenterZ=0 NormalX=0 NormalY=0 NormalZ=1 AngleXU=0 Radius=1.41421
FEATURE [PartDesign::Pocket] Pocket023
  BaseFeature = -> Pocket022
  Length = 10
  Length2 = 100
  Profile = -> Sketch039
  Type = 0
FEATURE [Sketcher::SketchObject] Sketch040
  MapMode = 5
  Placement = pos=(5,0,0) rot=(0.57735,-0.57735,-0.57735;2.0944rad)
  Support = -> [Pocket023]
  sketch-geometry (1):
    g0: Circle CenterX=41 CenterY=5 CenterZ=0 NormalX=0 NormalY=0 NormalZ=1 AngleXU=0 Radius=1.41421
FEATURE [PartDesign::Pocket] Pocket024
  BaseFeature = -> Pocket023
  Length = 10
  Length2 = 100
  Profile = -> Sketch040
  Type = 0
FEATURE [PartDesign::Body] Body
  Group = -> [Sketch,Pad,Sketch001,Pocket,Sketch002,Pocket001,Sketch003,Pocket002,Sketch004,Pocket003,Sketch005,Pocket004,Sketch006,Pocket005,Sketch007,Pocket006,Sketch008,Pocket007,Sketch009,Pocket008,Sketch010,Pocket009,Fillet,Fillet001,Fillet002,Fillet003,Fillet004,Fillet005,Fillet006,Fillet007,Fillet008,Fillet009,Fillet010,Fillet011,Fillet012,Fillet013,Fillet014,Fillet015,Fillet016,Fillet017,Fillet018,+102 more]
  Origin = -> Origin
  Tip = -> Pocket024
